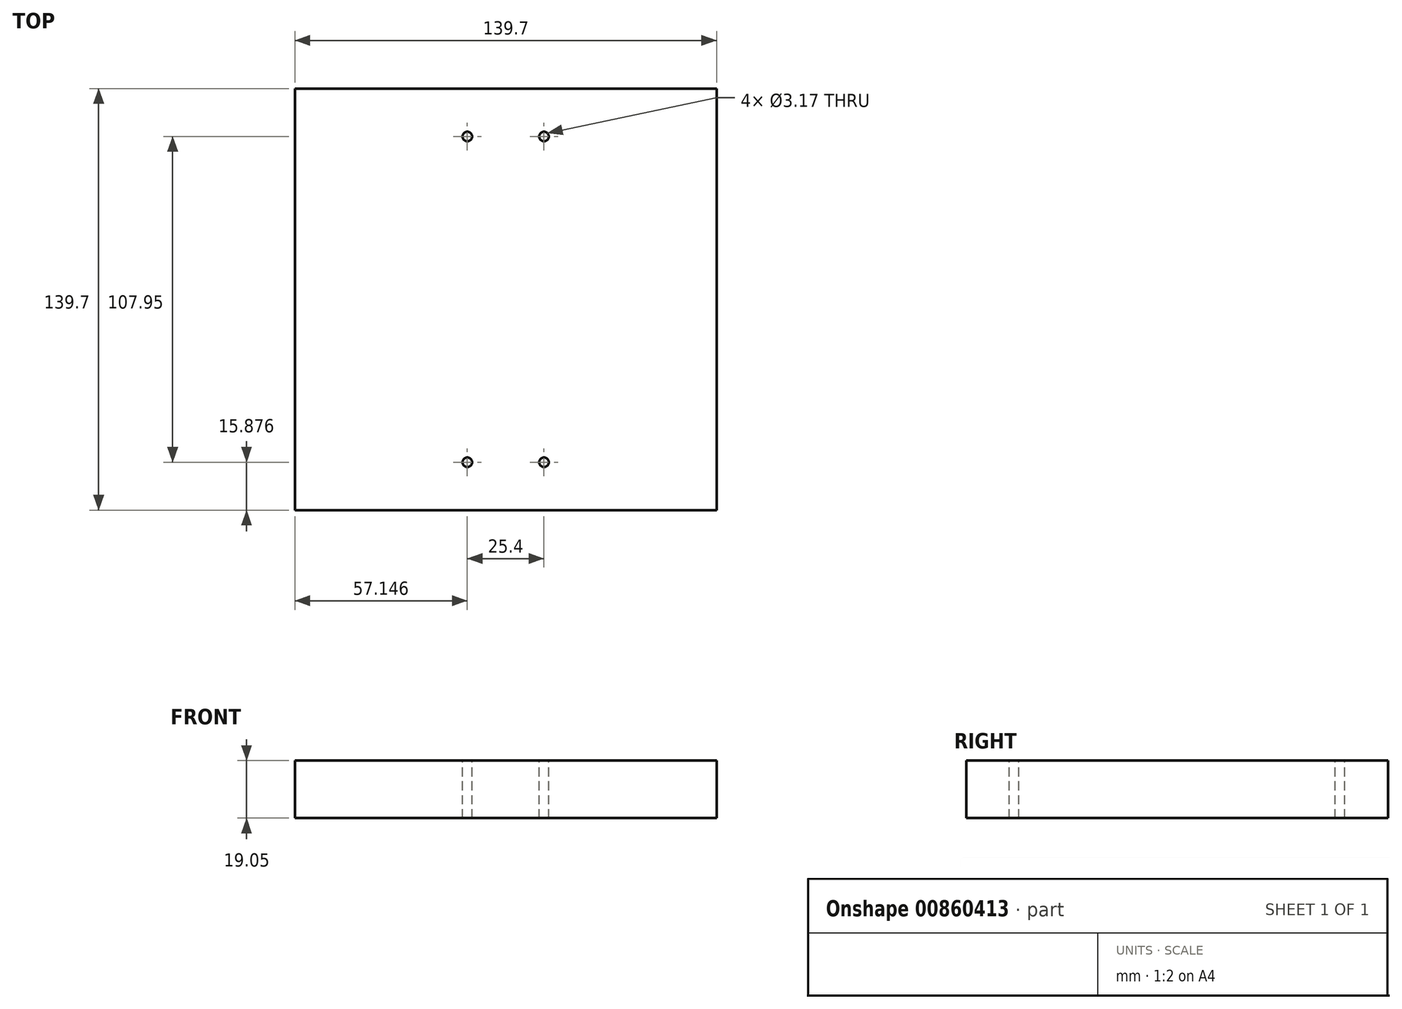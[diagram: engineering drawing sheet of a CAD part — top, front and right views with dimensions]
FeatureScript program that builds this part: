
annotation { "Feature Type Name" : "Feature", "Feature Type Description" : "" }
export const myFeature = defineFeature(function(context is Context, id is Id, definition is map)
    precondition{}
    {
        {
            var Q0;
            Q0=qCreatedBy(makeId("Top.planeOp"),FACE);
            var sketch = newSketch(context, id + "F0", { "sketchPlane" : qUnion([Q0])});
            skLineSegment(sketch, "E0.bottom", {"start": v(-107.84, 92.66) * mm, "end": v(31.86, 92.66) * mm});
            skLineSegment(sketch, "E0.top", {"start": v(-107.84, -47.04) * mm, "end": v(31.86, -47.04) * mm});
            skLineSegment(sketch, "E0.left", {"start": v(-107.84, 92.66) * mm, "end": v(-107.84, -47.04) * mm});
            skLineSegment(sketch, "E0.right", {"start": v(31.86, 92.66) * mm, "end": v(31.86, -47.04) * mm});
            skSolve(sketch);
        }
        {
            var Q0;
            Q0=makeQuery(id+"F0.imprint","IMPRINT",FACE,{"disambiguationData":[TD([[makeQuery(id+"F0.imprint","IMPRINT",EDGE,{"derivedFrom":sQuery(id+"F0.wireOp",EDGE,"E0.bottom")}),-1.0]])]});
            extrude(context, id + "F1", {"entities" : qUnion([Q0]), "depth" : 19.05 * mm, "offsetDistance" : 25.4 * mm});
        }
        {
            var Q0;
            Q0=makeQuery(id+"F1.opExtrude","CAP_FACE",FACE,{"disambiguationData":[OSD([sQuery(id+"F0.wireOp",EDGE,"E0.bottom"),sQuery(id+"F0.wireOp",EDGE,"E0.top"),sQuery(id+"F0.wireOp",EDGE,"E0.left"),sQuery(id+"F0.wireOp",EDGE,"E0.right")])],"isStart":false});
            var sketch = newSketch(context, id + "F2", { "sketchPlane" : qUnion([Q0])});
            skPoint(sketch, "E1", {"position": v(-50.7, 76.79) * mm});
            skPoint(sketch, "E2", {"position": v(-25.3, 76.79) * mm});
            skPoint(sketch, "E3", {"position": v(-50.7, -31.16) * mm});
            skPoint(sketch, "E4", {"position": v(-25.3, -31.16) * mm});
            skSolve(sketch);
        }
        {
            var Q0;
            Q0=sQuery(id+"F2.wireOp",VERTEX,"E3");
            var Q1;
            Q1=sQuery(id+"F2.wireOp",VERTEX,"E4");
            var Q2;
            Q2=sQuery(id+"F2.wireOp",VERTEX,"E1");
            var Q3;
            Q3=sQuery(id+"F2.wireOp",VERTEX,"E2");
            var Q4;
            Q4=makeQuery(id+"F1.opExtrude","SWEPT_BODY",BODY,{"disambiguationData":[OSD([sQuery(id+"F0.wireOp",EDGE,"E0.bottom"),sQuery(id+"F0.wireOp",EDGE,"E0.top"),sQuery(id+"F0.wireOp",EDGE,"E0.left"),sQuery(id+"F0.wireOp",EDGE,"E0.right")])]});
            hole(context, id + "F3", {"style" : HoleStyle.SIMPLE, "endStyle" : HoleEndStyle.THROUGH, "holeDiameter" : 3.17 * mm, "majorDiameter" : 6.35 * mm, "isTappedThrough" : true, "tappedDepth" : 12.7 * mm, "tapClearance" : 3, "locations" : qUnion([Q0, Q1, Q2, Q3]), "scope" : qUnion([Q4])});
        }
    });
